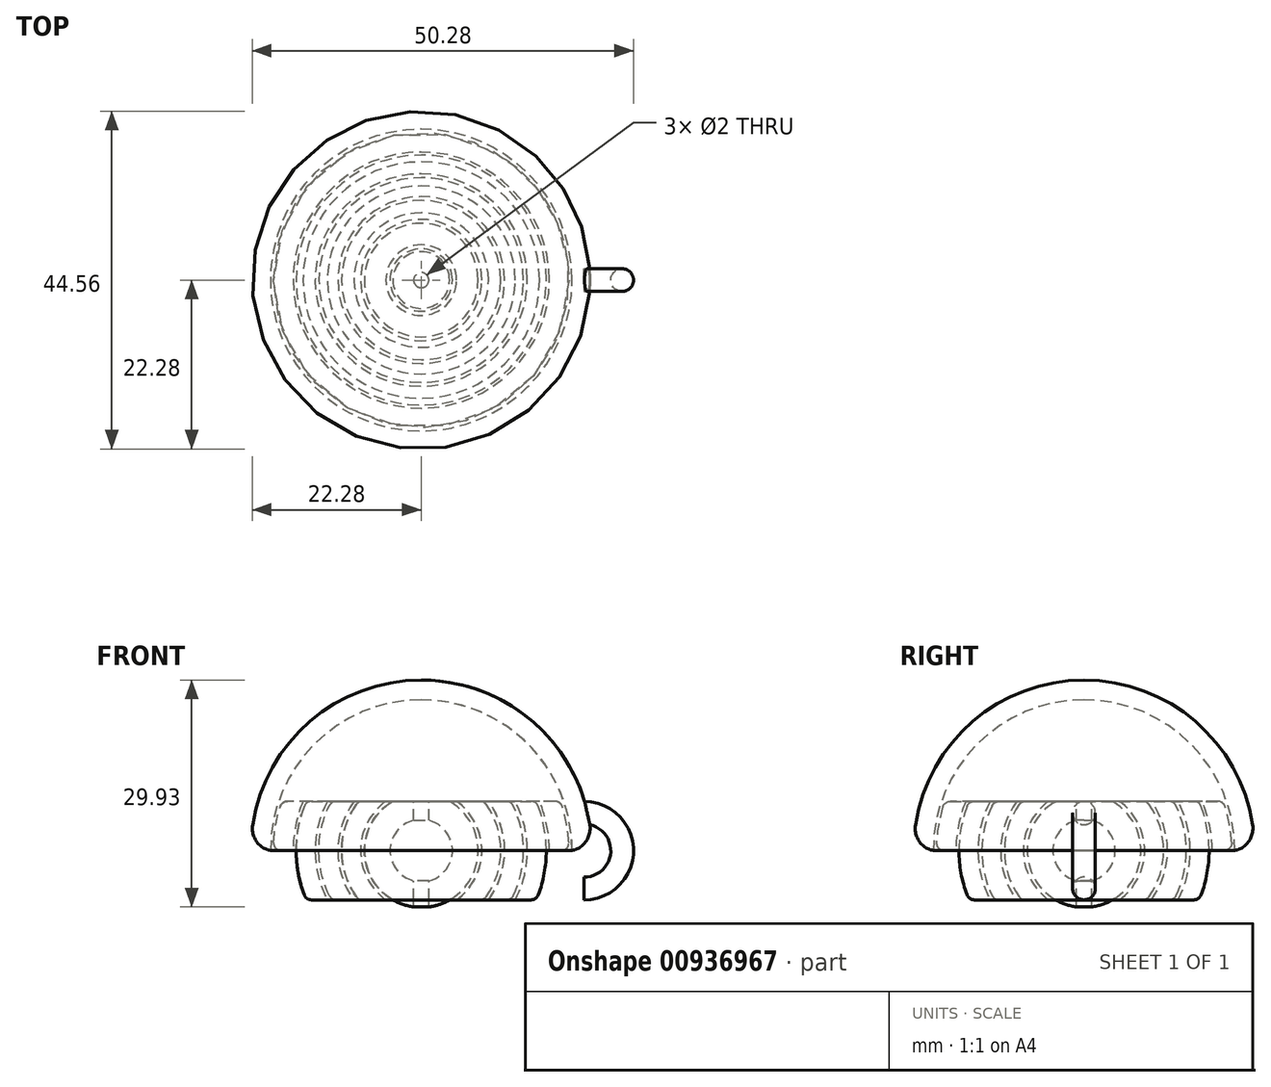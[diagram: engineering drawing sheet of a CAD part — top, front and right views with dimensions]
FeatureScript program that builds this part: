
annotation { "Feature Type Name" : "Feature", "Feature Type Description" : "" }
export const myFeature = defineFeature(function(context is Context, id is Id, definition is map)
    precondition{}
    {
        {
            var Q0;
            Q0=qCreatedBy(makeId("Front.planeOp"),FACE);
            var sketch = newSketch(context, id + "F0", { "sketchPlane" : qUnion([Q0])});
            skCircle(sketch, "E0", {"center": v(0, 0) * mm, "radius": 22.5 * mm});
            skCircle(sketch, "E1", {"center": v(0, 0) * mm, "radius": 19.9 * mm});
            skCircle(sketch, "E2", {"center": v(0, 0) * mm, "radius": 19.5 * mm});
            skCircle(sketch, "E3", {"center": v(0, 0) * mm, "radius": 16.9 * mm});
            skCircle(sketch, "E4", {"center": v(0, 0) * mm, "radius": 16.5 * mm});
            skCircle(sketch, "E5", {"center": v(0, 0) * mm, "radius": 14 * mm});
            skCircle(sketch, "E6", {"center": v(0, 0) * mm, "radius": 13.5 * mm});
            skCircle(sketch, "E7", {"center": v(0, 0) * mm, "radius": 11 * mm});
            skCircle(sketch, "E8", {"center": v(0, 0) * mm, "radius": 10.5 * mm});
            skCircle(sketch, "E9", {"center": v(0, 0) * mm, "radius": 8 * mm});
            skCircle(sketch, "E10", {"center": v(0, 0) * mm, "radius": 7.5 * mm});
            skCircle(sketch, "E11", {"center": v(0, 0) * mm, "radius": 4.11 * mm});
            skLineSegment(sketch, "E12", {"start": v(0, 24.67) * mm, "end": v(0, -27.98) * mm});
            skLineSegment(sketch, "E13", {"start": v(-21.54, 6.5) * mm, "end": v(21.54, 6.5) * mm});
            skLineSegment(sketch, "E14", {"start": v(-22.5, 0) * mm, "end": v(22.5, 0) * mm});
            skLineSegment(sketch, "E15.trimOffspring", {"start": v(-21.54, -6.5) * mm, "end": v(21.54, -6.5) * mm});
            skSolve(sketch);
        }
        {
            var Q0;
            {var subQ0=sQuery(id+"F0.wireOp",EDGE,"E13");var subQ1=sQuery(id+"F0.wireOp",EDGE,"E10");var subQ2=makeQuery(id+"F0.imprint","INTERSECT",VERTEX,{"disambiguationData":[OD(1.0)],"derivedFrom":[subQ1,subQ0]});Q0=makeQuery(id+"F0.imprint","IMPRINT",FACE,{"disambiguationData":[TD([[makeQuery(id+"F0.imprint","IMPRINT",EDGE,{"disambiguationData":[TD([[subQ2,-1.0]])],"derivedFrom":subQ1}),1.0]])]});}
            var Q1;
            {var subQ0=sQuery(id+"F0.wireOp",EDGE,"E14");var subQ1=sQuery(id+"F0.wireOp",EDGE,"E10");var subQ2=makeQuery(id+"F0.imprint","INTERSECT",VERTEX,{"disambiguationData":[OD(1.0)],"derivedFrom":[subQ1,subQ0]});Q1=makeQuery(id+"F0.imprint","IMPRINT",FACE,{"disambiguationData":[TD([[makeQuery(id+"F0.imprint","IMPRINT",EDGE,{"disambiguationData":[TD([[subQ2,-1.0]])],"derivedFrom":subQ1}),1.0]])]});}
            var Q2;
            {var subQ0=sQuery(id+"F0.wireOp",EDGE,"E12");var subQ1=sQuery(id+"F0.wireOp",EDGE,"E10");var subQ2=makeQuery(id+"F0.imprint","INTERSECT",VERTEX,{"disambiguationData":[OD(0.0)],"derivedFrom":[subQ1,subQ0]});Q2=makeQuery(id+"F0.imprint","IMPRINT",FACE,{"disambiguationData":[TD([[makeQuery(id+"F0.imprint","IMPRINT",EDGE,{"disambiguationData":[TD([[subQ2,-1.0]])],"derivedFrom":subQ1}),1.0]])]});}
            var Q3;
            Q3=sQuery(id+"F0.wireOp",EDGE,"E12");
            revolve(context, id + "F1", {"surfaceOperationType" : NewSurfaceOperationType.NEW, "entities" : qUnion([Q0, Q1, Q2]), "axis" : qUnion([Q3]), "revolveType" : RevolveType.FULL});
        }
        {
            var Q0;
            {var subQ0=sQuery(id+"F0.wireOp",EDGE,"E13");var subQ1=sQuery(id+"F0.wireOp",EDGE,"E8");var subQ2=makeQuery(id+"F0.imprint","INTERSECT",VERTEX,{"disambiguationData":[OD(1.0)],"derivedFrom":[subQ1,subQ0]});Q0=makeQuery(id+"F0.imprint","IMPRINT",FACE,{"disambiguationData":[TD([[makeQuery(id+"F0.imprint","IMPRINT",EDGE,{"disambiguationData":[TD([[subQ2,-1.0]])],"derivedFrom":subQ1}),1.0]])]});}
            var Q1;
            {var subQ0=sQuery(id+"F0.wireOp",EDGE,"E14");var subQ1=sQuery(id+"F0.wireOp",EDGE,"E8");var subQ2=makeQuery(id+"F0.imprint","INTERSECT",VERTEX,{"disambiguationData":[OD(1.0)],"derivedFrom":[subQ1,subQ0]});Q1=makeQuery(id+"F0.imprint","IMPRINT",FACE,{"disambiguationData":[TD([[makeQuery(id+"F0.imprint","IMPRINT",EDGE,{"disambiguationData":[TD([[subQ2,-1.0]])],"derivedFrom":subQ1}),1.0]])]});}
            var Q2;
            Q2=sQuery(id+"F0.wireOp",EDGE,"E12");
            revolve(context, id + "F2", {"surfaceOperationType" : NewSurfaceOperationType.NEW, "entities" : qUnion([Q0, Q1]), "axis" : qUnion([Q2]), "revolveType" : RevolveType.FULL});
        }
        {
            var Q0;
            {var subQ0=sQuery(id+"F0.wireOp",EDGE,"E13");var subQ1=sQuery(id+"F0.wireOp",EDGE,"E6");var subQ2=makeQuery(id+"F0.imprint","INTERSECT",VERTEX,{"disambiguationData":[OD(1.0)],"derivedFrom":[subQ1,subQ0]});Q0=makeQuery(id+"F0.imprint","IMPRINT",FACE,{"disambiguationData":[TD([[makeQuery(id+"F0.imprint","IMPRINT",EDGE,{"disambiguationData":[TD([[subQ2,-1.0]])],"derivedFrom":subQ1}),1.0]])]});}
            var Q1;
            {var subQ0=sQuery(id+"F0.wireOp",EDGE,"E14");var subQ1=sQuery(id+"F0.wireOp",EDGE,"E6");var subQ2=makeQuery(id+"F0.imprint","INTERSECT",VERTEX,{"disambiguationData":[OD(1.0)],"derivedFrom":[subQ1,subQ0]});Q1=makeQuery(id+"F0.imprint","IMPRINT",FACE,{"disambiguationData":[TD([[makeQuery(id+"F0.imprint","IMPRINT",EDGE,{"disambiguationData":[TD([[subQ2,-1.0]])],"derivedFrom":subQ1}),1.0]])]});}
            var Q2;
            Q2=sQuery(id+"F0.wireOp",EDGE,"E12");
            revolve(context, id + "F3", {"surfaceOperationType" : NewSurfaceOperationType.NEW, "entities" : qUnion([Q0, Q1]), "axis" : qUnion([Q2]), "revolveType" : RevolveType.FULL});
        }
        {
            var Q0;
            {var subQ0=sQuery(id+"F0.wireOp",EDGE,"E13");var subQ1=sQuery(id+"F0.wireOp",EDGE,"E4");var subQ2=makeQuery(id+"F0.imprint","INTERSECT",VERTEX,{"disambiguationData":[OD(1.0)],"derivedFrom":[subQ1,subQ0]});Q0=makeQuery(id+"F0.imprint","IMPRINT",FACE,{"disambiguationData":[TD([[makeQuery(id+"F0.imprint","IMPRINT",EDGE,{"disambiguationData":[TD([[subQ2,-1.0]])],"derivedFrom":subQ1}),1.0]])]});}
            var Q1;
            {var subQ0=sQuery(id+"F0.wireOp",EDGE,"E14");var subQ1=sQuery(id+"F0.wireOp",EDGE,"E4");var subQ2=makeQuery(id+"F0.imprint","INTERSECT",VERTEX,{"disambiguationData":[OD(1.0)],"derivedFrom":[subQ1,subQ0]});Q1=makeQuery(id+"F0.imprint","IMPRINT",FACE,{"disambiguationData":[TD([[makeQuery(id+"F0.imprint","IMPRINT",EDGE,{"disambiguationData":[TD([[subQ2,-1.0]])],"derivedFrom":subQ1}),1.0]])]});}
            var Q2;
            Q2=sQuery(id+"F0.wireOp",EDGE,"E12");
            revolve(context, id + "F4", {"surfaceOperationType" : NewSurfaceOperationType.NEW, "entities" : qUnion([Q0, Q1]), "axis" : qUnion([Q2]), "revolveType" : RevolveType.FULL});
        }
        {
            var Q0;
            {var subQ0=sQuery(id+"F0.wireOp",EDGE,"E13");var subQ1=sQuery(id+"F0.wireOp",EDGE,"E2");var subQ2=makeQuery(id+"F0.imprint","INTERSECT",VERTEX,{"disambiguationData":[OD(1.0)],"derivedFrom":[subQ1,subQ0]});Q0=makeQuery(id+"F0.imprint","IMPRINT",FACE,{"disambiguationData":[TD([[makeQuery(id+"F0.imprint","IMPRINT",EDGE,{"disambiguationData":[TD([[subQ2,-1.0]])],"derivedFrom":subQ1}),1.0]])]});}
            var Q1;
            {var subQ0=sQuery(id+"F0.wireOp",EDGE,"E14");var subQ1=sQuery(id+"F0.wireOp",EDGE,"E2");var subQ2=makeQuery(id+"F0.imprint","INTERSECT",VERTEX,{"disambiguationData":[OD(1.0)],"derivedFrom":[subQ1,subQ0]});Q1=makeQuery(id+"F0.imprint","IMPRINT",FACE,{"disambiguationData":[TD([[makeQuery(id+"F0.imprint","IMPRINT",EDGE,{"disambiguationData":[TD([[subQ2,-1.0]])],"derivedFrom":subQ1}),1.0]])]});}
            var Q2;
            Q2=sQuery(id+"F0.wireOp",EDGE,"E12");
            revolve(context, id + "F5", {"surfaceOperationType" : NewSurfaceOperationType.NEW, "entities" : qUnion([Q0, Q1]), "axis" : qUnion([Q2]), "revolveType" : RevolveType.FULL});
        }
        {
            var Q0;
            {var subQ0=sQuery(id+"F0.wireOp",EDGE,"E13");var subQ1=sQuery(id+"F0.wireOp",EDGE,"E0");var subQ2=makeQuery(id+"F0.imprint","INTERSECT",VERTEX,{"disambiguationData":[OD(0.0)],"derivedFrom":[subQ1,subQ0]});Q0=makeQuery(id+"F0.imprint","IMPRINT",FACE,{"disambiguationData":[TD([[makeQuery(id+"F0.imprint","IMPRINT",EDGE,{"disambiguationData":[TD([[subQ2,-1.0]])],"derivedFrom":subQ1}),1.0]])]});}
            var Q1;
            {var subQ0=sQuery(id+"F0.wireOp",EDGE,"E14");var subQ1=sQuery(id+"F0.wireOp",EDGE,"E0");var subQ2=makeQuery(id+"F0.imprint","INTERSECT",VERTEX,{"disambiguationData":[OD(0.0)],"derivedFrom":[subQ1,subQ0]});Q1=makeQuery(id+"F0.imprint","IMPRINT",FACE,{"disambiguationData":[TD([[makeQuery(id+"F0.imprint","IMPRINT",EDGE,{"disambiguationData":[TD([[subQ2,-1.0]])],"derivedFrom":subQ1}),1.0]])]});}
            var Q2;
            Q2=sQuery(id+"F0.wireOp",EDGE,"E12");
            revolve(context, id + "F6", {"surfaceOperationType" : NewSurfaceOperationType.NEW, "entities" : qUnion([Q0, Q1]), "axis" : qUnion([Q2]), "revolveType" : RevolveType.FULL});
        }
        {
            var Q0;
            Q0=qCreatedBy(makeId("Right.planeOp"),FACE);
            var Q1;
            Q1 = qBodyType(qCreatedBy(id + "F8" ,EDGE), BodyType.WIRE);
            cPlane(context, id + "F7", {"entities" : qUnion([Q0, Q1]), "cplaneType" : CPlaneType.OFFSET, "offset" : 21.5 * mm, "width" : 150 * mm, "height" : 150 * mm});
        }
        {
            var Q0;
            Q0=qCreatedBy(id+"F7.planeOp",FACE);
            var sketch = newSketch(context, id + "F8", { "sketchPlane" : qUnion([Q0])});
            skCircle(sketch, "E16", {"center": v(0, 5) * mm, "radius": 1.5 * mm});
            skPoint(sketch, "E16.first.point", {"position": v(0, 6.5) * mm});
            skPoint(sketch, "E16.second.point", {"position": v(0, 3.5) * mm});
            skPoint(sketch, "E16.third.point", {"position": v(1.27, 4.2) * mm});
            skLineSegment(sketch, "E17", {"start": v(-33.93, 0) * mm, "end": v(45.1, 0) * mm});
            skSolve(sketch);
        }
        {
            var Q0;
            Q0 = qSketchRegion(id + "F8", true);
            var Q1;
            Q1=sQuery(id+"F8.wireOp",EDGE,"E17");
            revolve(context, id + "F9", {"operationType" : NewBodyOperationType.ADD, "surfaceOperationType" : NewSurfaceOperationType.NEW, "entities" : qUnion([Q0]), "axis" : qUnion([Q1]), "revolveType" : RevolveType.ONE_DIRECTION, "angle" : 180 * degree});
        }
        {
            var Q0;
            Q0=qCreatedBy(makeId("Top.planeOp"),FACE);
            var Q1;
            Q1=qCreatedBy(makeId("Top.planeOp"),FACE);
            var sketch = newSketch(context, id + "F10", { "sketchPlane" : qUnion([Q0, Q1])});
            skCircle(sketch, "E18", {"center": v(0, 0) * mm, "radius": 1 * mm});
            skSolve(sketch);
        }
        {
            var Q0;
            Q0 = qSketchRegion(id + "F10", true);
            extrude(context, id + "F11", {"entities" : qUnion([Q0]), "operationType" : NewBodyOperationType.REMOVE, "endBound" : BoundingType.SYMMETRIC, "oppositeDirection" : true, "depth" : 25 * mm, "offsetDistance" : 25 * mm});
        }
        {
            var Q0;
            Q0=makeQuery(id+"F6.opRevolve","SWEPT_EDGE",EDGE,{"disambiguationData":[OSD([sQuery(id+"F0.wireOp",EDGE,"E0"),sQuery(id+"F0.wireOp",EDGE,"E13")])]});
            var Q1;
            Q1=makeQuery(id+"F6.opRevolve","SWEPT_EDGE",EDGE,{"disambiguationData":[OSD([sQuery(id+"F0.wireOp",EDGE,"E0"),sQuery(id+"F0.wireOp",EDGE,"E15.trimOffspring")])]});
            fillet(context, id + "F12", {"entities" : qUnion([Q0, Q1]), "radius" : 3 * mm, "tangentPropagation" : true, "allowEdgeOverflow" : false});
        }
        {
            var Q0;
            Q0=makeQuery(id+"F5.opRevolve","SWEPT_EDGE",EDGE,{"disambiguationData":[OSD([sQuery(id+"F0.wireOp",EDGE,"E2"),sQuery(id+"F0.wireOp",EDGE,"E13")])]});
            fillet(context, id + "F13", {"entities" : qUnion([Q0]), "radius" : 1 * mm, "tangentPropagation" : true, "allowEdgeOverflow" : false});
        }
        {
            var Q0;
            Q0=makeQuery(id+"F4.opRevolve","SWEPT_EDGE",EDGE,{"disambiguationData":[OSD([sQuery(id+"F0.wireOp",EDGE,"E4"),sQuery(id+"F0.wireOp",EDGE,"E13")])]});
            var Q1;
            Q1=makeQuery(id+"F3.opRevolve","SWEPT_EDGE",EDGE,{"disambiguationData":[OSD([sQuery(id+"F0.wireOp",EDGE,"E6"),sQuery(id+"F0.wireOp",EDGE,"E13")])]});
            var Q2;
            Q2=makeQuery(id+"F2.opRevolve","SWEPT_EDGE",EDGE,{"disambiguationData":[OSD([sQuery(id+"F0.wireOp",EDGE,"E8"),sQuery(id+"F0.wireOp",EDGE,"E13")])]});
            var Q3;
            Q3=makeQuery(id+"F1.opRevolve","SWEPT_EDGE",EDGE,{"disambiguationData":[OSD([sQuery(id+"F0.wireOp",EDGE,"E10"),sQuery(id+"F0.wireOp",EDGE,"E13")])]});
            var Q4;
            Q4=makeQuery(id+"F5.opRevolve","SWEPT_EDGE",EDGE,{"disambiguationData":[OSD([sQuery(id+"F0.wireOp",EDGE,"E2"),sQuery(id+"F0.wireOp",EDGE,"E15.trimOffspring")])]});
            var Q5;
            Q5=makeQuery(id+"F4.opRevolve","SWEPT_EDGE",EDGE,{"disambiguationData":[OSD([sQuery(id+"F0.wireOp",EDGE,"E4"),sQuery(id+"F0.wireOp",EDGE,"E15.trimOffspring")])]});
            var Q6;
            Q6=makeQuery(id+"F3.opRevolve","SWEPT_EDGE",EDGE,{"disambiguationData":[OSD([sQuery(id+"F0.wireOp",EDGE,"E6"),sQuery(id+"F0.wireOp",EDGE,"E15.trimOffspring")])]});
            var Q7;
            Q7=makeQuery(id+"F2.opRevolve","SWEPT_EDGE",EDGE,{"disambiguationData":[OSD([sQuery(id+"F0.wireOp",EDGE,"E8"),sQuery(id+"F0.wireOp",EDGE,"E15.trimOffspring")])]});
            var Q8;
            Q8=makeQuery(id+"F1.opRevolve","SWEPT_EDGE",EDGE,{"disambiguationData":[OSD([sQuery(id+"F0.wireOp",EDGE,"E10"),sQuery(id+"F0.wireOp",EDGE,"E15.trimOffspring")])]});
            fillet(context, id + "F14", {"entities" : qUnion([Q0, Q1, Q2, Q3, Q4, Q5, Q6, Q7, Q8]), "radius" : 1 * mm, "tangentPropagation" : true, "allowEdgeOverflow" : false});
        }
        {
            var Q0;
            Q0=makeQuery(id+"F3.opRevolve","SWEPT_FACE",FACE,{"disambiguationData":[OSD([sQuery(id+"F0.wireOp",EDGE,"E13")])]});
            var Q1;
            Q1=makeQuery(id+"F2.opRevolve","SWEPT_FACE",FACE,{"disambiguationData":[OSD([sQuery(id+"F0.wireOp",EDGE,"E13")])]});
            var Q2;
            Q2=makeQuery(id+"F2.opRevolve","SWEPT_FACE",FACE,{"disambiguationData":[OSD([sQuery(id+"F0.wireOp",EDGE,"E13")])]});
            var Q3;
            Q3=makeQuery(id+"F3.opRevolve","SWEPT_FACE",FACE,{"disambiguationData":[OSD([sQuery(id+"F0.wireOp",EDGE,"E13")])]});
            var Q4;
            Q4=makeQuery(id+"F2.opRevolve","SWEPT_FACE",FACE,{"disambiguationData":[OSD([sQuery(id+"F0.wireOp",EDGE,"E13")])]});
            cPlane(context, id + "F15", {"entities" : qUnion([Q0, Q1, Q2, Q3, Q4]), "cplaneType" : CPlaneType.MID_PLANE, "offset" : 25 * mm, "width" : 150 * mm, "height" : 150 * mm});
        }
        {
            var Q0;
            Q0=qCreatedBy(id+"F15.planeOp",FACE);
            cPlane(context, id + "F16", {"entities" : qUnion([Q0]), "cplaneType" : CPlaneType.OFFSET, "offset" : 0.5 * mm, "width" : 150 * mm, "height" : 150 * mm});
        }
    });
